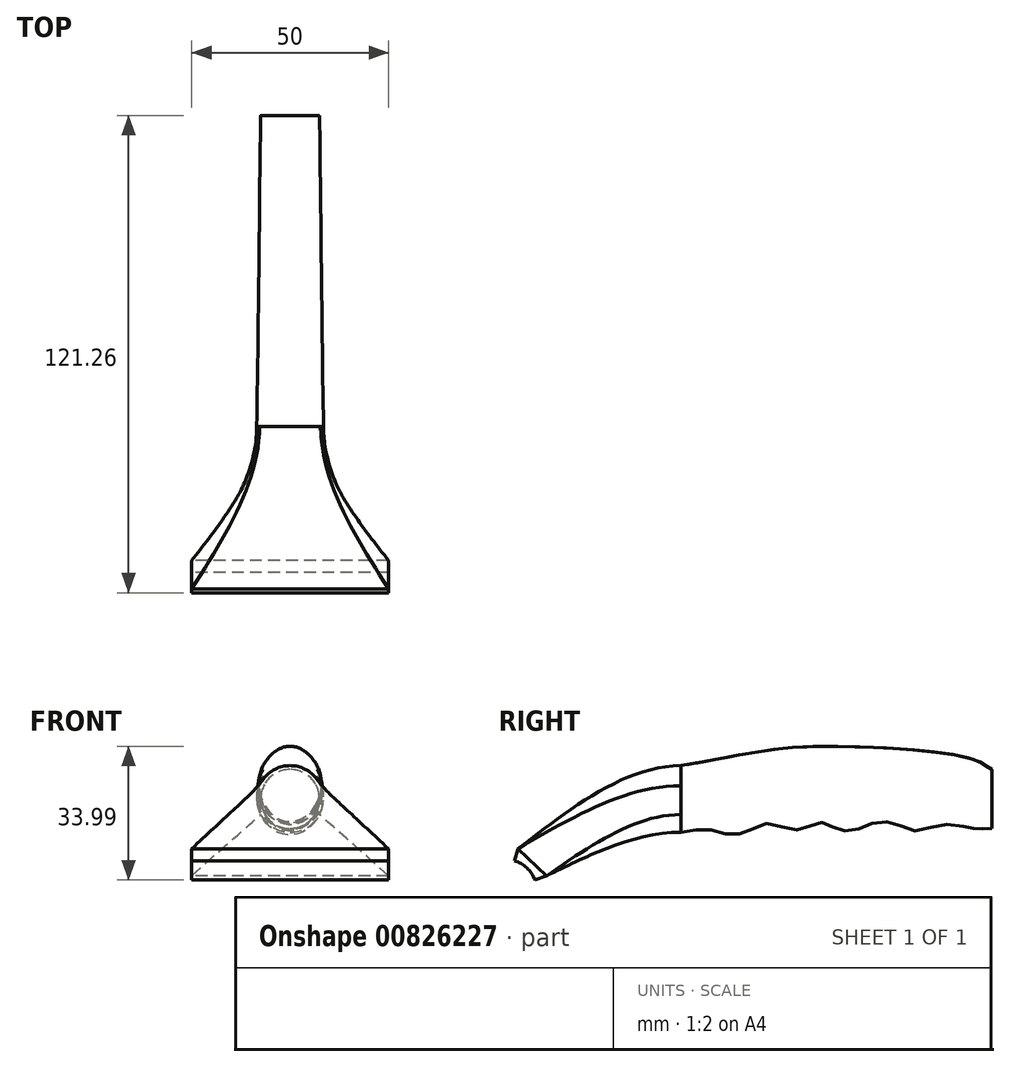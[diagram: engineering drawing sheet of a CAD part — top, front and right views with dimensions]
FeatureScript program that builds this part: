
annotation { "Feature Type Name" : "Feature", "Feature Type Description" : "" }
export const myFeature = defineFeature(function(context is Context, id is Id, definition is map)
    precondition{}
    {
        {
            var Q0;
            Q0=qCreatedBy(makeId("Right.planeOp"),FACE);
            var sketch = newSketch(context, id + "F0", { "sketchPlane" : qUnion([Q0])});
            skLineSegment(sketch, "E0", {"start": v(0, 19.13) * mm, "end": v(0, -13.83) * mm, "construction": true});
            skLineSegment(sketch, "E1", {"start": v(0, 0) * mm, "end": v(3.27, 10.69) * mm});
            skLineSegment(sketch, "E2", {"start": v(0, 0) * mm, "end": v(10.5, 3.82) * mm});
            skLineSegment(sketch, "E3", {"start": v(44.6, 14.86) * mm, "end": v(44.6, 31.8) * mm, "construction": true});
            skLineSegment(sketch, "E4", {"start": v(3.27, 10.69) * mm, "end": v(10.5, 3.82) * mm});
            skCircle(sketch, "E5", {"center": v(0, 0) * mm, "radius": 8 * mm});
            skSolve(sketch);
        }
        {
            var Q0;
            {var subQ0=sQuery(id+"F0.wireOp",EDGE,"E2");var subQ1=sQuery(id+"F0.wireOp",EDGE,"E1");var subQ2=makeQuery(id+"F0.imprint","INTERSECT",VERTEX,{"derivedFrom":[subQ1,subQ0]});Q0=makeQuery(id+"F0.imprint","IMPRINT",FACE,{"disambiguationData":[TD([[makeQuery(id+"F0.imprint","IMPRINT",EDGE,{"disambiguationData":[TD([[subQ2,-1.0]])],"derivedFrom":subQ1}),1.0]])]});}
            var Q1;
            {var subQ0=sQuery(id+"F0.wireOp",EDGE,"E2");var subQ1=sQuery(id+"F0.wireOp",EDGE,"E1");var subQ2=makeQuery(id+"F0.imprint","INTERSECT",VERTEX,{"derivedFrom":[subQ1,subQ0]});Q1=makeQuery(id+"F0.imprint","IMPRINT",FACE,{"disambiguationData":[TD([[makeQuery(id+"F0.imprint","IMPRINT",EDGE,{"disambiguationData":[TD([[subQ2,-1.0]])],"derivedFrom":subQ1}),-1.0]])]});}
            extrude(context, id + "F1", {"entities" : qUnion([Q0, Q1]), "endBound" : BoundingType.SYMMETRIC, "depth" : 200 * mm, "offsetDistance" : 25 * mm});
        }
        {
            var Q0;
            {var subQ0=sQuery(id+"F0.wireOp",EDGE,"E4");Q0=makeQuery(id+"F0.imprint","IMPRINT",FACE,{"disambiguationData":[TD([[makeQuery(id+"F0.imprint","IMPRINT",EDGE,{"derivedFrom":subQ0}),-1.0]])]});}
            extrude(context, id + "F2", {"entities" : qUnion([Q0]), "operationType" : NewBodyOperationType.ADD, "endBound" : BoundingType.SYMMETRIC, "depth" : 50 * mm, "offsetDistance" : 25 * mm});
        }
        {
            var Q0;
            Q0=sQuery(id+"F0.wireOp",EDGE,"E3");
            cPlane(context, id + "F3", {"entities" : qUnion([Q0]), "cplaneType" : CPlaneType.LINE_ANGLE, "offset" : 25 * mm, "angle" : 90 * degree, "width" : 150 * mm, "height" : 150 * mm});
        }
        {
            var Q0;
            Q0=qCreatedBy(id+"F3.planeOp",FACE);
            var sketch = newSketch(context, id + "F4", { "sketchPlane" : qUnion([Q0])});
            skPoint(sketch, "E6.0", {"position": v(0, 31.8) * mm});
            skPoint(sketch, "E7.0", {"position": v(0, 19.13) * mm});
            skPoint(sketch, "E8.0", {"position": v(0, 14.86) * mm});
            skPoint(sketch, "E9", {"position": v(0, 23.33) * mm});
            skLineSegment(sketch, "E10", {"start": v(-7.5, 19.38) * mm, "end": v(7.5, 19.38) * mm, "construction": true});
            skLineSegment(sketch, "E11", {"start": v(-7.76, 26.72) * mm, "end": v(7.76, 26.72) * mm, "construction": true});
            skArc(sketch, "E12", {"start": v(7.76, 26.72) * mm, "mid": v(0, 31.8) * mm, "end": v(-7.76, 26.72) * mm});
            skArc(sketch, "E13", {"start": v(-7.76, 26.72) * mm, "mid": v(-8.46, 23.02) * mm, "end": v(-7.5, 19.38) * mm});
            skArc(sketch, "E14", {"start": v(7.5, 19.38) * mm, "mid": v(8.46, 23.02) * mm, "end": v(7.76, 26.72) * mm});
            skArc(sketch, "E15", {"start": v(-7.5, 19.38) * mm, "mid": v(0, 14.86) * mm, "end": v(7.5, 19.38) * mm});
            skSolve(sketch);
        }
        {
            var Q1;
            Q1=makeQuery(id+"F2.opExtrude","SWEPT_FACE",FACE,{"disambiguationData":[OSD([sQuery(id+"F0.wireOp",EDGE,"E4")])]});
            var Q2;
            Q2=makeQuery(id+"F4.imprint","IMPRINT",FACE,{"disambiguationData":[TD([[makeQuery(id+"F4.imprint","IMPRINT",EDGE,{"derivedFrom":sQuery(id+"F4.wireOp",EDGE,"E12")}),1.0]])]});
            var Q3;
            Q3=makeQuery(id+"F2.opExtrude","CAP_VERTEX",VERTEX,{"disambiguationData":[OSD([sQuery(id+"F0.wireOp",EDGE,"E1"),sQuery(id+"F0.wireOp",EDGE,"E4")])],"isStart":false});
            var Q4;
            Q4=sQuery(id+"F4.wireOp",VERTEX,"E11.start");
            var Q5;
            Q5=makeQuery(id+"F2.opExtrude","CAP_VERTEX",VERTEX,{"disambiguationData":[OSD([sQuery(id+"F0.wireOp",EDGE,"E1"),sQuery(id+"F0.wireOp",EDGE,"E4")])],"isStart":true});
            var Q6;
            Q6=sQuery(id+"F4.wireOp",VERTEX,"E11.end");
            var Q7;
            Q7=makeQuery(id+"F2.opExtrude","CAP_VERTEX",VERTEX,{"disambiguationData":[OSD([sQuery(id+"F0.wireOp",EDGE,"E2"),sQuery(id+"F0.wireOp",EDGE,"E4")])],"isStart":false});
            var Q8;
            Q8=sQuery(id+"F4.wireOp",VERTEX,"E10.start");
            var Q9;
            Q9=makeQuery(id+"F2.opExtrude","CAP_VERTEX",VERTEX,{"disambiguationData":[OSD([sQuery(id+"F0.wireOp",EDGE,"E2"),sQuery(id+"F0.wireOp",EDGE,"E4")])],"isStart":true});
            var Q10;
            Q10=sQuery(id+"F4.wireOp",VERTEX,"E10.end");
            loft(context, id + "F5", {"operationType" : NewBodyOperationType.ADD, "endCondition" : LoftEndDerivativeType.NORMAL_TO_PROFILE, "endMagnitude" : 1, "sheetProfilesArray" : [{ "sheetProfileEntities" : qUnion([Q1]) }, { "sheetProfileEntities" : qUnion([Q2]) }], "connections" : [{ "connectionEntities" : qUnion([Q3, Q4, Q5, Q6, Q7, Q8, Q9, Q10]), "connectionEdgeQueries" : qUnion([]), "connectionEdgeParameters" : [] }]});
        }
        {
            var Q0;
            Q0=qCreatedBy(id+"F3.planeOp",FACE);
            cPlane(context, id + "F6", {"entities" : qUnion([Q0]), "cplaneType" : CPlaneType.OFFSET, "offset" : 79 * mm, "width" : 150 * mm, "height" : 150 * mm});
        }
        {
            var Q0;
            Q0=qCreatedBy(id+"F6.planeOp",FACE);
            var sketch = newSketch(context, id + "F7", { "sketchPlane" : qUnion([Q0])});
            skPoint(sketch, "E16.0", {"position": v(0, 23.33) * mm});
            skCircle(sketch, "E17", {"center": v(0, 23.33) * mm, "radius": 7.48 * mm});
            skSolve(sketch);
        }
        {
            var Q0;
            Q0=qCreatedBy(makeId("Right.planeOp"),FACE);
            var sketch = newSketch(context, id + "F8", { "sketchPlane" : qUnion([Q0])});
            skFitSpline(sketch, "E18", {"points": [v(44.6, 14.86) * mm, v(52.25, 15.5) * mm, v(57.57, 14.19) * mm, v(63.45, 15.98) * mm, v(67.4, 17.07) * mm, v(73.98, 15.43) * mm, v(80.44, 17.33) * mm, v(84.67, 15.51) * mm, v(89.7, 15.64) * mm, v(94.4, 17.48) * mm, v(99.88, 16.8) * mm, v(104.97, 15.16) * mm, v(110.32, 16.75) * mm, v(119.2, 15.85) * mm, v(123.6, 15.84) * mm], "startDerivative": vector(115.17, 19.03) * mm, "endDerivative": vector(43.27, 8.67) * mm});
            skFitSpline(sketch, "E19", {"points": [v(44.6, 31.8) * mm, v(49.95, 32.72) * mm, v(59.16, 34.43) * mm, v(73.34, 36.41) * mm, v(93.87, 36.4) * mm, v(119.83, 33.04) * mm, v(123.6, 30.81) * mm], "startDerivative": vector(62.6, 11.47) * mm, "endDerivative": vector(27.16, -9.57) * mm});
            skSolve(sketch);
        }
        {
            var Q1;
            Q1=makeQuery(id+"F5.opLoft","CAP_FACE",FACE,{"disambiguationData":[OSD([makeQuery(id+"F4.imprint","IMPRINT",FACE,{"disambiguationData":[TD([[makeQuery(id+"F4.imprint","IMPRINT",EDGE,{"derivedFrom":sQuery(id+"F4.wireOp",EDGE,"E12")}),1.0]])]})])],"isStart":true});
            var Q2;
            Q2=makeQuery(id+"F7.imprint","IMPRINT",FACE,{"disambiguationData":[TD([[makeQuery(id+"F7.imprint","IMPRINT",EDGE,{"derivedFrom":sQuery(id+"F7.wireOp",EDGE,"E17")}),1.0]])]});
            var Q3;
            Q3=sQuery(id+"F8.wireOp",EDGE,"E19");
            var Q4;
            Q4=sQuery(id+"F8.wireOp",EDGE,"E18");
            loft(context, id + "F9", {"operationType" : NewBodyOperationType.ADD, "addGuides" : true, "sheetProfilesArray" : [{ "sheetProfileEntities" : qUnion([Q1]) }, { "sheetProfileEntities" : qUnion([Q2]) }], "guidesArray" : [{ "guideEntities" : qUnion([Q3]), "guideDerivativeType" : LoftGuideDerivativeType.DEFAULT, "guideDerivativeMagnitude" : 1 }, { "guideEntities" : qUnion([Q4]), "guideDerivativeType" : LoftGuideDerivativeType.DEFAULT, "guideDerivativeMagnitude" : 1 }]});
        }
        {
            var Q0;
            Q0=makeQuery(id+"F1.opExtrude","CAP_FACE",FACE,{"disambiguationData":[OSD([sQuery(id+"F0.wireOp",EDGE,"E5")])],"isStart":false});
            extrude(context, id + "F10", {"entities" : qUnion([Q0]), "operationType" : NewBodyOperationType.REMOVE, "oppositeDirection" : true, "depth" : 239 * mm, "offsetDistance" : 25 * mm});
        }
    });
